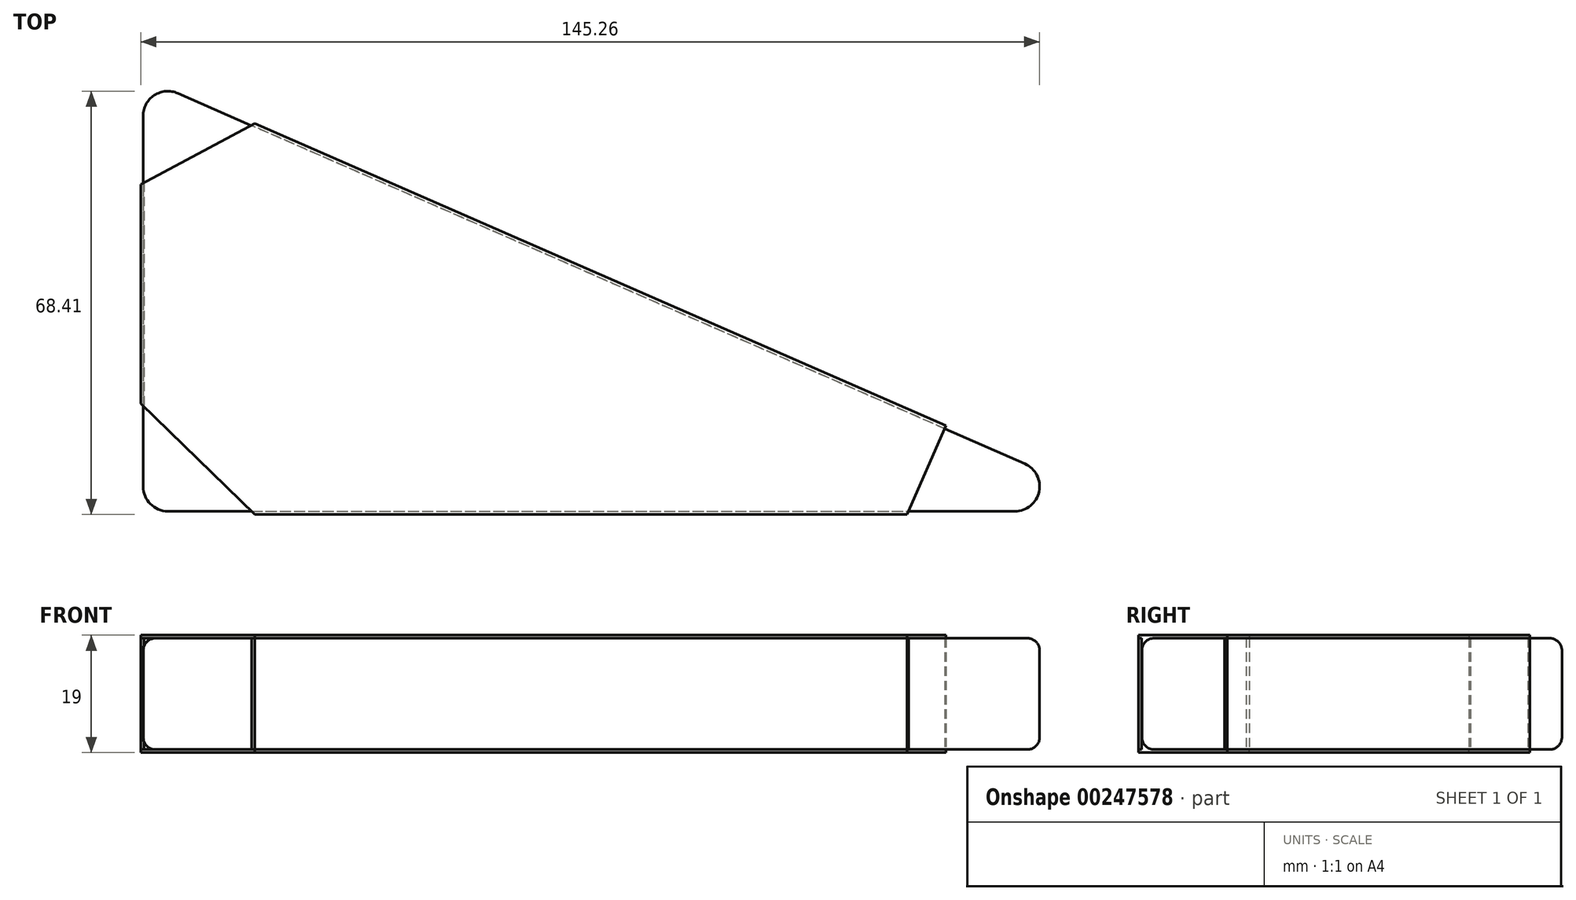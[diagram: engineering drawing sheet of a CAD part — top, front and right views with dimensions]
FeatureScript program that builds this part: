
annotation { "Feature Type Name" : "Feature", "Feature Type Description" : "" }
export const myFeature = defineFeature(function(context is Context, id is Id, definition is map)
    precondition{}
    {
        {
            var Q0;
            Q0=qCreatedBy(makeId("Top.planeOp"),FACE);
            var sketch = newSketch(context, id + "F0", { "sketchPlane" : qUnion([Q0])});
            skLineSegment(sketch, "E0", {"start": v(-96.46, 40.25) * mm, "end": v(-96.46, -29.75) * mm});
            skLineSegment(sketch, "E1", {"start": v(-96.46, -29.75) * mm, "end": v(63.54, -29.75) * mm});
            skLineSegment(sketch, "E2", {"start": v(63.54, -29.75) * mm, "end": v(-96.46, 40.25) * mm});
            skSolve(sketch);
        }
        {
            var Q0;
            Q0=qCreatedBy(makeId("Top.planeOp"),FACE);
            var sketch = newSketch(context, id + "F1", { "sketchPlane" : qUnion([Q0])});
            skLineSegment(sketch, "E3", {"start": v(-96.35, 23.36) * mm, "end": v(-96.35, -12.87) * mm});
            skLineSegment(sketch, "E4", {"start": v(-78.96, -29.77) * mm, "end": v(27.23, -29.77) * mm});
            skLineSegment(sketch, "E5", {"start": v(33.08, -16.4) * mm, "end": v(-79, 32.64) * mm});
            skLineSegment(sketch, "E6.0", {"start": v(-96.85, 23.09) * mm, "end": v(-96.85, -12.39) * mm});
            skLineSegment(sketch, "E6.1", {"start": v(33.28, -15.94) * mm, "end": v(-78.44, 32.94) * mm});
            skLineSegment(sketch, "E6.2", {"start": v(-78.44, -30.27) * mm, "end": v(27.01, -30.27) * mm});
            skLineSegment(sketch, "E7", {"start": v(-96.85, 23.09) * mm, "end": v(-78.44, 32.94) * mm});
            skLineSegment(sketch, "E8", {"start": v(33.28, -15.94) * mm, "end": v(27.01, -30.27) * mm});
            skLineSegment(sketch, "E9", {"start": v(-96.85, -12.39) * mm, "end": v(-78.44, -30.27) * mm});
            skSolve(sketch);
        }
        {
            var Q0;
            Q0 = qSketchRegion(id + "F0", true);
            extrude(context, id + "F2", {"entities" : qUnion([Q0]), "depth" : 18 * mm});
        }
        {
            var Q0;
            {var subQ0=sQuery(id+"F1.wireOp",EDGE,"E4");Q0=makeQuery(id+"F1.imprint","IMPRINT",FACE,{"disambiguationData":[TD([[makeQuery(id+"F1.imprint","IMPRINT",EDGE,{"derivedFrom":subQ0}),-1.0]])]});}
            var Q1;
            {var subQ0=sQuery(id+"F1.wireOp",EDGE,"E5");Q1=makeQuery(id+"F1.imprint","IMPRINT",FACE,{"disambiguationData":[TD([[makeQuery(id+"F1.imprint","IMPRINT",EDGE,{"derivedFrom":subQ0}),-1.0]])]});}
            var Q2;
            {var subQ2=sQuery(id+"F1.wireOp",EDGE,"E3");Q2=makeQuery(id+"F1.imprint","IMPRINT",FACE,{"disambiguationData":[TD([[makeQuery(id+"F1.imprint","IMPRINT",EDGE,{"derivedFrom":subQ2}),1.0]])]});}
            var Q3;
            {var subQ0=sQuery(id+"F1.wireOp",EDGE,"E3");Q3=makeQuery(id+"F1.imprint","IMPRINT",FACE,{"disambiguationData":[TD([[makeQuery(id+"F1.imprint","IMPRINT",EDGE,{"derivedFrom":subQ0}),-1.0]])]});}
            extrude(context, id + "F3", {"entities" : qUnion([Q0, Q1, Q2, Q3]), "depth" : 18.5 * mm, "hasSecondDirection" : true, "secondDirectionOppositeDirection" : false, "secondDirectionDepth" : 18 * mm});
        }
        {
            var Q0;
            Q0 = qSketchRegion(id + "F1", true);
            extrude(context, id + "F4", {"entities" : qUnion([Q0]), "oppositeDirection" : true, "depth" : 0.5 * mm});
        }
        {
            var Q0;
            {var subQ0=sQuery(id+"F1.wireOp",EDGE,"E5");Q0=makeQuery(id+"F1.imprint","IMPRINT",FACE,{"disambiguationData":[TD([[makeQuery(id+"F1.imprint","IMPRINT",EDGE,{"derivedFrom":subQ0}),-1.0]])]});}
            var Q1;
            {var subQ0=sQuery(id+"F1.wireOp",EDGE,"E3");Q1=makeQuery(id+"F1.imprint","IMPRINT",FACE,{"disambiguationData":[TD([[makeQuery(id+"F1.imprint","IMPRINT",EDGE,{"derivedFrom":subQ0}),-1.0]])]});}
            var Q2;
            {var subQ0=sQuery(id+"F1.wireOp",EDGE,"E4");Q2=makeQuery(id+"F1.imprint","IMPRINT",FACE,{"disambiguationData":[TD([[makeQuery(id+"F1.imprint","IMPRINT",EDGE,{"derivedFrom":subQ0}),-1.0]])]});}
            extrude(context, id + "F5", {"entities" : qUnion([Q0, Q1, Q2]), "depth" : 18 * mm});
        }
        {
            var Q0;
            Q0=makeQuery(id+"F2.opExtrude","SWEPT_EDGE",EDGE,{"disambiguationData":[OSD([sQuery(id+"F0.wireOp",EDGE,"E1"),sQuery(id+"F0.wireOp",EDGE,"E2")])]});
            var Q1;
            Q1=makeQuery(id+"F2.opExtrude","SWEPT_EDGE",EDGE,{"disambiguationData":[OSD([sQuery(id+"F0.wireOp",EDGE,"E0"),sQuery(id+"F0.wireOp",EDGE,"E2")])]});
            var Q2;
            Q2=makeQuery(id+"F2.opExtrude","SWEPT_EDGE",EDGE,{"disambiguationData":[OSD([sQuery(id+"F0.wireOp",EDGE,"E0"),sQuery(id+"F0.wireOp",EDGE,"E1")])]});
            fillet(context, id + "F6", {"entities" : qUnion([Q0, Q1, Q2]), "radius" : 4 * mm, "tangentPropagation" : true, "allowEdgeOverflow" : false});
        }
        {
            var Q0;
            Q0=makeQuery(id+"F2.opExtrude","CAP_EDGE",EDGE,{"disambiguationData":[OSD([sQuery(id+"F0.wireOp",EDGE,"E0")])],"isStart":false});
            var Q1;
            Q1=makeQuery(id+"F2.opExtrude","CAP_EDGE",EDGE,{"disambiguationData":[OSD([sQuery(id+"F0.wireOp",EDGE,"E1")])],"isStart":false});
            var Q2;
            {var subQ0=sQuery(id+"F0.wireOp",EDGE,"E1");var subQ1=sQuery(id+"F0.wireOp",EDGE,"E0");Q2=makeQuery(id+"F6.opFillet","BLEND_EDGE",EDGE,{"blendedFrom":[makeQuery(id+"F2.opExtrude","SWEPT_EDGE",EDGE,{"disambiguationData":[OSD([subQ1,subQ0])]}),makeQuery(id+"F2.opExtrude","CAP_FACE",FACE,{"disambiguationData":[OSD([subQ1,subQ0,sQuery(id+"F0.wireOp",EDGE,"E2")])],"isStart":false})],"blendedInto":[makeQuery(id+"F2.opExtrude","CAP_FACE",FACE,{"disambiguationData":[OSD([subQ1,subQ0,sQuery(id+"F0.wireOp",EDGE,"E2")])],"isStart":false})]});}
            var Q3;
            {var subQ0=sQuery(id+"F0.wireOp",EDGE,"E2");var subQ1=sQuery(id+"F0.wireOp",EDGE,"E1");Q3=makeQuery(id+"F6.opFillet","BLEND_EDGE",EDGE,{"blendedFrom":[makeQuery(id+"F2.opExtrude","SWEPT_EDGE",EDGE,{"disambiguationData":[OSD([subQ1,subQ0])]}),makeQuery(id+"F2.opExtrude","CAP_FACE",FACE,{"disambiguationData":[OSD([sQuery(id+"F0.wireOp",EDGE,"E0"),subQ1,subQ0])],"isStart":false})],"blendedInto":[makeQuery(id+"F2.opExtrude","CAP_FACE",FACE,{"disambiguationData":[OSD([sQuery(id+"F0.wireOp",EDGE,"E0"),subQ1,subQ0])],"isStart":false})]});}
            var Q4;
            Q4=makeQuery(id+"F2.opExtrude","CAP_EDGE",EDGE,{"disambiguationData":[OSD([sQuery(id+"F0.wireOp",EDGE,"E2")])],"isStart":false});
            var Q5;
            {var subQ0=sQuery(id+"F0.wireOp",EDGE,"E2");var subQ1=sQuery(id+"F0.wireOp",EDGE,"E0");Q5=makeQuery(id+"F6.opFillet","BLEND_EDGE",EDGE,{"blendedFrom":[makeQuery(id+"F2.opExtrude","SWEPT_EDGE",EDGE,{"disambiguationData":[OSD([subQ1,subQ0])]}),makeQuery(id+"F2.opExtrude","CAP_FACE",FACE,{"disambiguationData":[OSD([subQ1,sQuery(id+"F0.wireOp",EDGE,"E1"),subQ0])],"isStart":false})],"blendedInto":[makeQuery(id+"F2.opExtrude","CAP_FACE",FACE,{"disambiguationData":[OSD([subQ1,sQuery(id+"F0.wireOp",EDGE,"E1"),subQ0])],"isStart":false})]});}
            var Q6;
            Q6=makeQuery(id+"F2.opExtrude","CAP_EDGE",EDGE,{"disambiguationData":[OSD([sQuery(id+"F0.wireOp",EDGE,"E2")])],"isStart":true});
            var Q7;
            {var subQ0=sQuery(id+"F0.wireOp",EDGE,"E2");var subQ1=sQuery(id+"F0.wireOp",EDGE,"E0");Q7=makeQuery(id+"F6.opFillet","BLEND_EDGE",EDGE,{"blendedFrom":[makeQuery(id+"F2.opExtrude","SWEPT_EDGE",EDGE,{"disambiguationData":[OSD([subQ1,subQ0])]}),makeQuery(id+"F2.opExtrude","CAP_FACE",FACE,{"disambiguationData":[OSD([subQ1,sQuery(id+"F0.wireOp",EDGE,"E1"),subQ0])],"isStart":true})],"blendedInto":[makeQuery(id+"F2.opExtrude","CAP_FACE",FACE,{"disambiguationData":[OSD([subQ1,sQuery(id+"F0.wireOp",EDGE,"E1"),subQ0])],"isStart":true})]});}
            var Q8;
            Q8=makeQuery(id+"F2.opExtrude","CAP_EDGE",EDGE,{"disambiguationData":[OSD([sQuery(id+"F0.wireOp",EDGE,"E0")])],"isStart":true});
            var Q9;
            {var subQ0=sQuery(id+"F0.wireOp",EDGE,"E1");var subQ1=sQuery(id+"F0.wireOp",EDGE,"E0");Q9=makeQuery(id+"F6.opFillet","BLEND_EDGE",EDGE,{"blendedFrom":[makeQuery(id+"F2.opExtrude","SWEPT_EDGE",EDGE,{"disambiguationData":[OSD([subQ1,subQ0])]}),makeQuery(id+"F2.opExtrude","CAP_FACE",FACE,{"disambiguationData":[OSD([subQ1,subQ0,sQuery(id+"F0.wireOp",EDGE,"E2")])],"isStart":true})],"blendedInto":[makeQuery(id+"F2.opExtrude","CAP_FACE",FACE,{"disambiguationData":[OSD([subQ1,subQ0,sQuery(id+"F0.wireOp",EDGE,"E2")])],"isStart":true})]});}
            var Q10;
            Q10=makeQuery(id+"F2.opExtrude","CAP_EDGE",EDGE,{"disambiguationData":[OSD([sQuery(id+"F0.wireOp",EDGE,"E1")])],"isStart":true});
            var Q11;
            {var subQ0=sQuery(id+"F0.wireOp",EDGE,"E2");var subQ1=sQuery(id+"F0.wireOp",EDGE,"E1");Q11=makeQuery(id+"F6.opFillet","BLEND_EDGE",EDGE,{"blendedFrom":[makeQuery(id+"F2.opExtrude","SWEPT_EDGE",EDGE,{"disambiguationData":[OSD([subQ1,subQ0])]}),makeQuery(id+"F2.opExtrude","CAP_FACE",FACE,{"disambiguationData":[OSD([sQuery(id+"F0.wireOp",EDGE,"E0"),subQ1,subQ0])],"isStart":true})],"blendedInto":[makeQuery(id+"F2.opExtrude","CAP_FACE",FACE,{"disambiguationData":[OSD([sQuery(id+"F0.wireOp",EDGE,"E0"),subQ1,subQ0])],"isStart":true})]});}
            fillet(context, id + "F7", {"entities" : qUnion([Q0, Q1, Q2, Q3, Q4, Q5, Q6, Q7, Q8, Q9, Q10, Q11]), "radius" : 2 * mm, "tangentPropagation" : true, "allowEdgeOverflow" : false});
        }
    });
